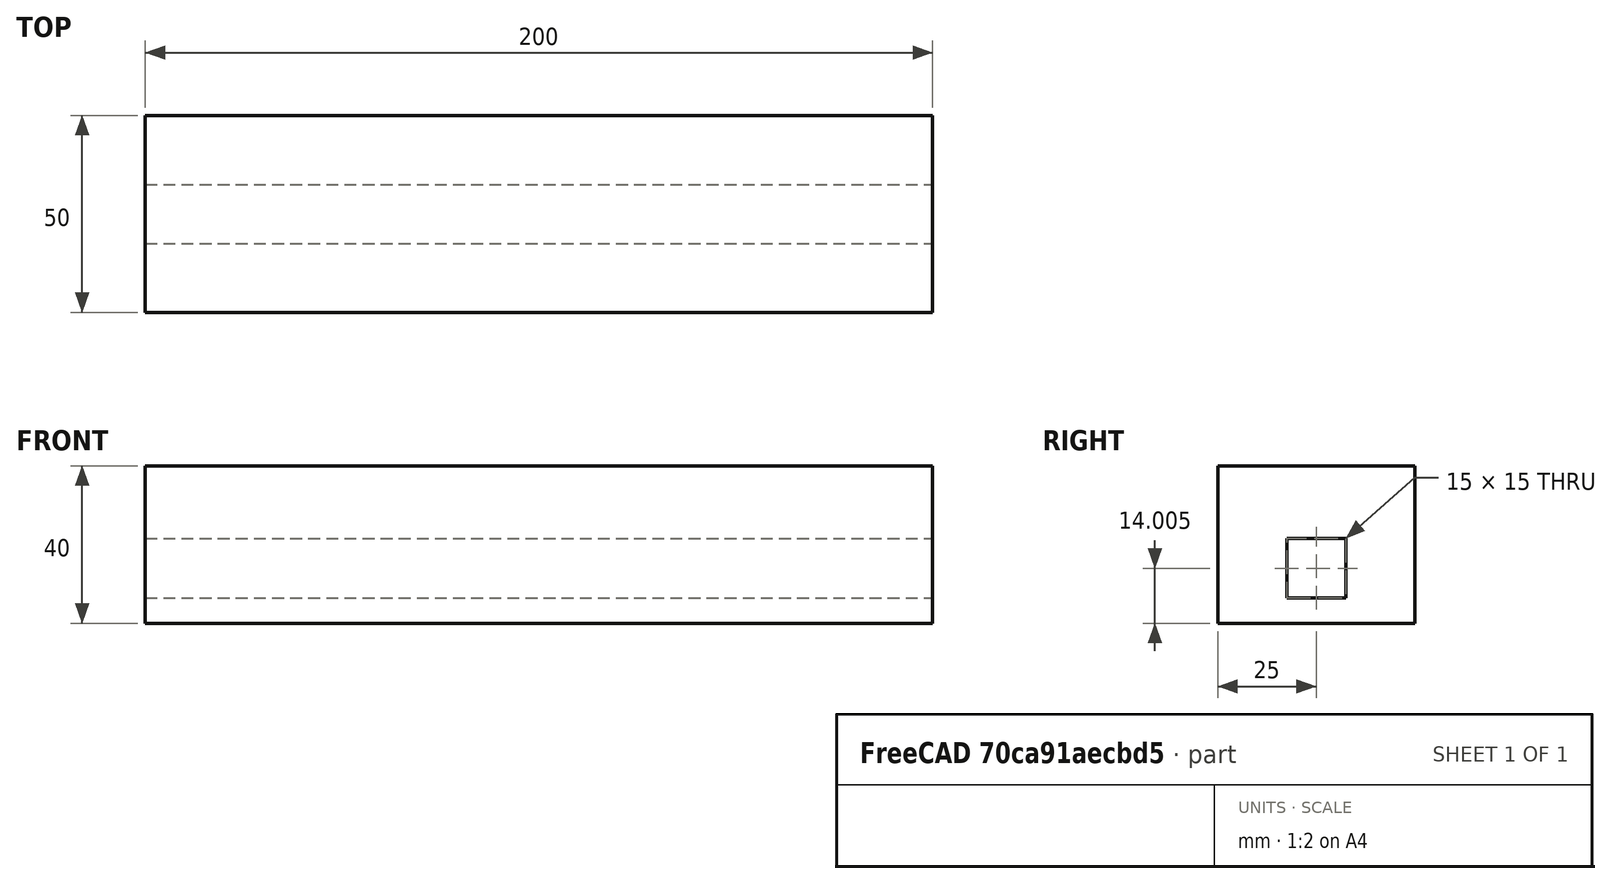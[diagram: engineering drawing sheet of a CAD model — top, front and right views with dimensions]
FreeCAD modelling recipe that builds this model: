
FCSTD DOCUMENT  (FreeCAD 1.0R39319 (Git))
Label: FirstArm
License: All rights reserved
LicenseURL: https://en.wikipedia.org/wiki/All_rights_reserved
objects: Sketcher::SketchObject×1, PartDesign::Pad×1, PartDesign::Body×1
note: 6 computed .brp shape members not serialized (recipe doc carries the construction recipe); baked Part::Feature solids carry a one-line shape summary decoded from their .brp

FEATURE [Sketcher::SketchObject] Sketch015
  ArcFitTolerance = 1e-06
  AttachmentSupport = -> [YZ_Plane004]
  FullyConstrained = false
  MakeInternals = false
  MapMode = 5
  Placement = pos=(0,0,0) rot=(0.57735,0.57735,0.57735;2.0944rad)
  sketch-geometry (8):
    g0: LineSegment StartX=-7.5 StartY=1.49431 StartZ=0 EndX=-7.5 EndY=-13.5057 EndZ=0
    g1: LineSegment StartX=-7.5 StartY=-13.5057 StartZ=0 EndX=7.5 EndY=-13.5057 EndZ=0
    g2: LineSegment StartX=7.5 StartY=-13.5057 StartZ=0 EndX=7.5 EndY=1.49431 EndZ=0
    g3: LineSegment StartX=7.5 StartY=1.49431 StartZ=0 EndX=-7.5 EndY=1.49431 EndZ=0
    g4: LineSegment StartX=-25 StartY=19.9943 StartZ=0 EndX=-25 EndY=-20.0057 EndZ=0
    g5: LineSegment StartX=-25 StartY=-20.0057 StartZ=0 EndX=25 EndY=-20.0057 EndZ=0
    g6: LineSegment StartX=25 StartY=-20.0057 StartZ=0 EndX=25 EndY=19.9943 EndZ=0
    g7: LineSegment StartX=25 StartY=19.9943 StartZ=0 EndX=-25 EndY=19.9943 EndZ=0
  constraints (23):
    c: Coincident(g0,g1)
    c: Coincident(g1,g2)
    c: Coincident(g2,g3)
    c: Coincident(g3,g0)
    c: Vertical(g0)
    c: Vertical(g2)
    c: Horizontal(g1)
    c: Horizontal(g3)
    c: Coincident(g4,g5)
    c: Coincident(g5,g6)
    c: Coincident(g6,g7)
    c: Coincident(g7,g4)
    c: Vertical(g4)
    c: Vertical(g6)
    c: Horizontal(g5)
    c: Horizontal(g7)
    c: DistanceX(g3,g3) = 15
    c: DistanceY(g2,g2) = 15
    c: Distance(g-2,g0) = 7.5
    c: Distance(g5,g1) = 6.5
    c: Distance(g-2,g6) = 25
    c: Distance(g-2,g4) = 25
    c: DistanceY(g6,g6) = 40
FEATURE [PartDesign::Pad] Pad008
  Direction = (1,0,0)
  Length = 200
  Length2 = 10
  Placement = pos=(0,0,0) rot=(1,1,1;2.0944rad)
  Profile = -> Sketch015
  ReferenceAxis = -> Sketch015 [N_Axis]
  Refine = true
  Suppressed = false
  Type = 0
FEATURE [PartDesign::Body] Body004  label="FirstArm"
  AllowCompound = false
  Group = -> [Sketch015,Pad008]
  Origin = -> Origin004
  Placement = pos=(28.7228,-8.4e-15,42.0005) rot=(0,0,1;0rad)
  Tip = -> Pad008
